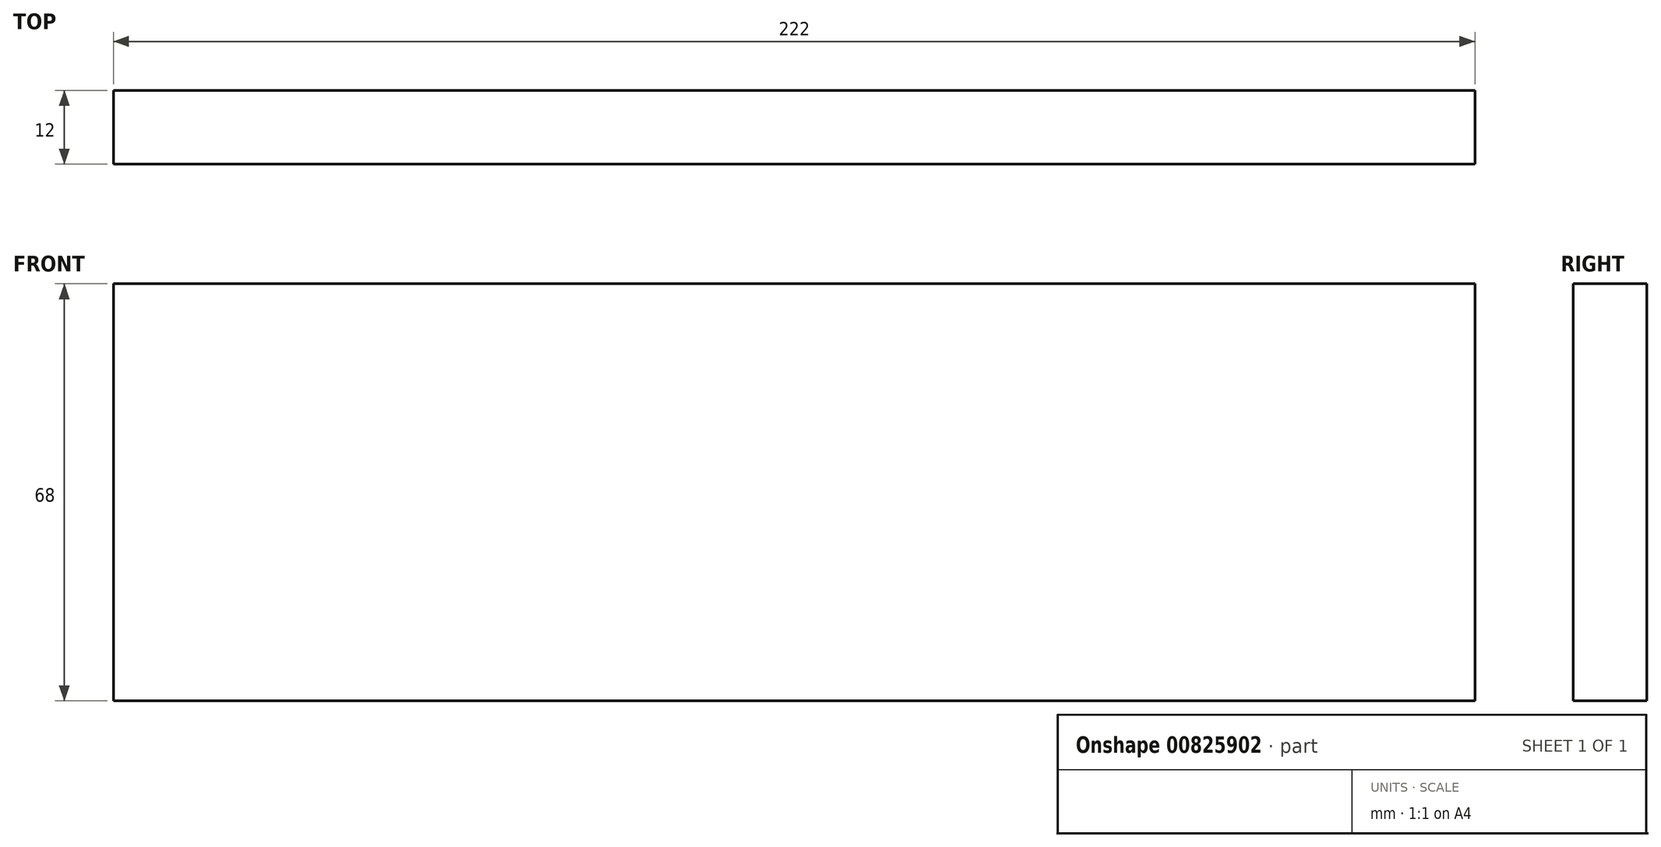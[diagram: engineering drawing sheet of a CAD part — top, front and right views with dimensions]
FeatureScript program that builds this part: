
annotation { "Feature Type Name" : "Feature", "Feature Type Description" : "" }
export const myFeature = defineFeature(function(context is Context, id is Id, definition is map)
    precondition{}
    {
        {
            var Q0;
            Q0=qCreatedBy(makeId("Right.planeOp"),FACE);
            var sketch = newSketch(context, id + "F0", { "sketchPlane" : qUnion([Q0])});
            skLineSegment(sketch, "E0.bottom", {"start": v(-111, 34) * mm, "end": v(111, 34) * mm});
            skLineSegment(sketch, "E0.top", {"start": v(-111, -34) * mm, "end": v(111, -34) * mm});
            skLineSegment(sketch, "E0.left", {"start": v(-111, 34) * mm, "end": v(-111, -34) * mm});
            skLineSegment(sketch, "E0.right", {"start": v(111, 34) * mm, "end": v(111, -34) * mm});
            skPoint(sketch, "E0.middle", {"position": v(0, 0) * mm});
            skSolve(sketch);
        }
        {
            var Q0;
            Q0 = qSketchRegion(id + "F0", true);
            extrude(context, id + "F1", {"entities" : qUnion([Q0]), "depth" : 12 * mm, "offsetDistance" : 25.4 * mm});
        }
        {
            var Q0;
            Q0=makeQuery(id+"F1.opExtrude","SWEPT_FACE",FACE,{"disambiguationData":[OSD([sQuery(id+"F0.wireOp",EDGE,"E0.left")])]});
            var sketch = newSketch(context, id + "F2", { "sketchPlane" : qUnion([Q0])});
            skLineSegment(sketch, "E1.bottom", {"start": v(0, 23.88) * mm, "end": v(3, 23.88) * mm});
            skLineSegment(sketch, "E1.top", {"start": v(0, 21.64) * mm, "end": v(3, 21.64) * mm});
            skLineSegment(sketch, "E1.left", {"start": v(0, 23.88) * mm, "end": v(0, 21.64) * mm});
            skLineSegment(sketch, "E1.right", {"start": v(3, 23.88) * mm, "end": v(3, 21.64) * mm});
            skSolve(sketch);
        }
        {
            var Q0;
            Q0 = qSketchRegion(id + "F2", true);
            extrude(context, id + "F3", {"entities" : qUnion([Q0]), "operationType" : NewBodyOperationType.REMOVE, "oppositeDirection" : true, "depth" : 2230 * mm, "offsetDistance" : 25.4 * mm});
        }
        {
            var Q0;
            Q0=makeQuery(id+"F1.opExtrude","SWEPT_BODY",BODY,{"disambiguationData":[OSD([sQuery(id+"F0.wireOp",EDGE,"E0.bottom"),sQuery(id+"F0.wireOp",EDGE,"E0.top"),sQuery(id+"F0.wireOp",EDGE,"E0.left"),sQuery(id+"F0.wireOp",EDGE,"E0.right")])]});
            deleteBodies(context, id + "F4", {"entities" : qUnion([Q0])});
        }
        {
            var Q0;
            Q0=qCreatedBy(makeId("Right.planeOp"),FACE);
            var sketch = newSketch(context, id + "F5", { "sketchPlane" : qUnion([Q0])});
            skLineSegment(sketch, "E2.bottom", {"start": v(111, 34) * mm, "end": v(-111, 34) * mm});
            skLineSegment(sketch, "E2.top", {"start": v(111, -34) * mm, "end": v(-111, -34) * mm});
            skLineSegment(sketch, "E2.left", {"start": v(111, 34) * mm, "end": v(111, -34) * mm});
            skLineSegment(sketch, "E2.right", {"start": v(-111, 34) * mm, "end": v(-111, -34) * mm});
            skPoint(sketch, "E2.middle", {"position": v(0, 0) * mm});
            skSolve(sketch);
        }
        {
            var Q0;
            Q0 = qSketchRegion(id + "F5", true);
            extrude(context, id + "F6", {"entities" : qUnion([Q0]), "depth" : 12 * mm, "offsetDistance" : 25.4 * mm});
        }
        {
            var Q0;
            Q0=makeQuery(id+"F6.opExtrude","CAP_FACE",FACE,{"disambiguationData":[OSD([sQuery(id+"F5.wireOp",EDGE,"E2.bottom"),sQuery(id+"F5.wireOp",EDGE,"E2.top"),sQuery(id+"F5.wireOp",EDGE,"E2.left"),sQuery(id+"F5.wireOp",EDGE,"E2.right")])],"isStart":true});
            var sketch = newSketch(context, id + "F7", { "sketchPlane" : qUnion([Q0])});
            skLineSegment(sketch, "E3.bottom", {"start": v(-101, 34) * mm, "end": v(-98, 34) * mm});
            skLineSegment(sketch, "E3.top", {"start": v(-101, 27.68) * mm, "end": v(-98, 27.68) * mm});
            skLineSegment(sketch, "E3.left", {"start": v(-101, 34) * mm, "end": v(-101, 27.68) * mm});
            skLineSegment(sketch, "E3.right", {"start": v(-98, 34) * mm, "end": v(-98, 27.68) * mm});
            skSolve(sketch);
        }
        {
            var Q0;
            Q0 = qSketchRegion(id + "F7", true);
            extrude(context, id + "F8", {"entities" : qUnion([Q0]), "operationType" : NewBodyOperationType.REMOVE, "oppositeDirection" : true, "depth" : 25.4 * mm, "offsetDistance" : 25.4 * mm});
        }
        {
            var Q0;
            Q0=makeQuery(id+"F6.opExtrude","SWEPT_FACE",FACE,{"disambiguationData":[OSD([sQuery(id+"F5.wireOp",EDGE,"E2.right")])]});
            var sketch = newSketch(context, id + "F9", { "sketchPlane" : qUnion([Q0])});
            skLineSegment(sketch, "E4.bottom", {"start": v(12, 24) * mm, "end": v(9, 24) * mm});
            skLineSegment(sketch, "E4.top", {"start": v(12, 21) * mm, "end": v(9, 21) * mm});
            skLineSegment(sketch, "E4.left", {"start": v(12, 24) * mm, "end": v(12, 21) * mm});
            skLineSegment(sketch, "E4.right", {"start": v(9, 24) * mm, "end": v(9, 21) * mm});
            skSolve(sketch);
        }
        {
            var Q0;
            Q0 = qSketchRegion(id + "F9", true);
            extrude(context, id + "F10", {"entities" : qUnion([Q0]), "operationType" : NewBodyOperationType.REMOVE, "oppositeDirection" : true, "depth" : 300 * mm, "offsetDistance" : 25.4 * mm});
        }
        {
            var Q0;
            {var subQ0=sQuery(id+"F5.wireOp",EDGE,"E2.right");var subQ1=sQuery(id+"F5.wireOp",EDGE,"E2.left");var subQ2=sQuery(id+"F5.wireOp",EDGE,"E2.bottom");Q0=makeQuery(id+"F10.boolean.opBoolean","SPLIT",FACE,{"disambiguationData":[TD([makeQuery(id+"F6.opExtrude","SWEPT_FACE",FACE,{"disambiguationData":[OSD([subQ2])]})])],"derivedFrom":makeQuery(id+"F6.opExtrude","CAP_FACE",FACE,{"disambiguationData":[OSD([subQ2,sQuery(id+"F5.wireOp",EDGE,"E2.top"),subQ1,subQ0])],"isStart":false})});}
            var sketch = newSketch(context, id + "F11", { "sketchPlane" : qUnion([Q0])});
            skLineSegment(sketch, "E5.bottom", {"start": v(101, 27.68) * mm, "end": v(98, 27.68) * mm});
            skLineSegment(sketch, "E5.top", {"start": v(101, 34) * mm, "end": v(98, 34) * mm});
            skLineSegment(sketch, "E5.left", {"start": v(101, 27.68) * mm, "end": v(101, 34) * mm});
            skLineSegment(sketch, "E5.right", {"start": v(98, 27.68) * mm, "end": v(98, 34) * mm});
            skSolve(sketch);
        }
        {
            var Q0;
            Q0 = qSketchRegion(id + "F11", true);
            extrude(context, id + "F12", {"entities" : qUnion([Q0]), "depth" : -12 * mm, "offsetDistance" : 25.4 * mm});
        }
        {
            var Q0;
            Q0=makeQuery(id+"F6.opExtrude","SWEPT_BODY",BODY,{"disambiguationData":[OSD([sQuery(id+"F5.wireOp",EDGE,"E2.bottom"),sQuery(id+"F5.wireOp",EDGE,"E2.top"),sQuery(id+"F5.wireOp",EDGE,"E2.left"),sQuery(id+"F5.wireOp",EDGE,"E2.right")])]});
            deleteBodies(context, id + "F13", {"entities" : qUnion([Q0])});
        }
        {
            var Q0;
            Q0=makeQuery(id+"F12.opExtrude","SWEPT_BODY",BODY,{"disambiguationData":[OSD([sQuery(id+"F11.wireOp",EDGE,"E5.bottom"),sQuery(id+"F11.wireOp",EDGE,"E5.top"),sQuery(id+"F11.wireOp",EDGE,"E5.left"),sQuery(id+"F11.wireOp",EDGE,"E5.right")])]});
            deleteBodies(context, id + "F14", {"entities" : qUnion([Q0])});
        }
        {
            var Q0;
            Q0=qCreatedBy(makeId("Front.planeOp"),FACE);
            var sketch = newSketch(context, id + "F15", { "sketchPlane" : qUnion([Q0])});
            skLineSegment(sketch, "E6.bottom", {"start": v(-111, 34) * mm, "end": v(111, 34) * mm});
            skLineSegment(sketch, "E6.top", {"start": v(-111, -34) * mm, "end": v(111, -34) * mm});
            skLineSegment(sketch, "E6.left", {"start": v(-111, 34) * mm, "end": v(-111, -34) * mm});
            skLineSegment(sketch, "E6.right", {"start": v(111, 34) * mm, "end": v(111, -34) * mm});
            skPoint(sketch, "E6.middle", {"position": v(0, 0) * mm});
            skSolve(sketch);
        }
        {
            var Q0;
            Q0 = qSketchRegion(id + "F15", true);
            extrude(context, id + "F16", {"entities" : qUnion([Q0]), "depth" : 12 * mm, "offsetDistance" : 25.4 * mm});
        }
    });
